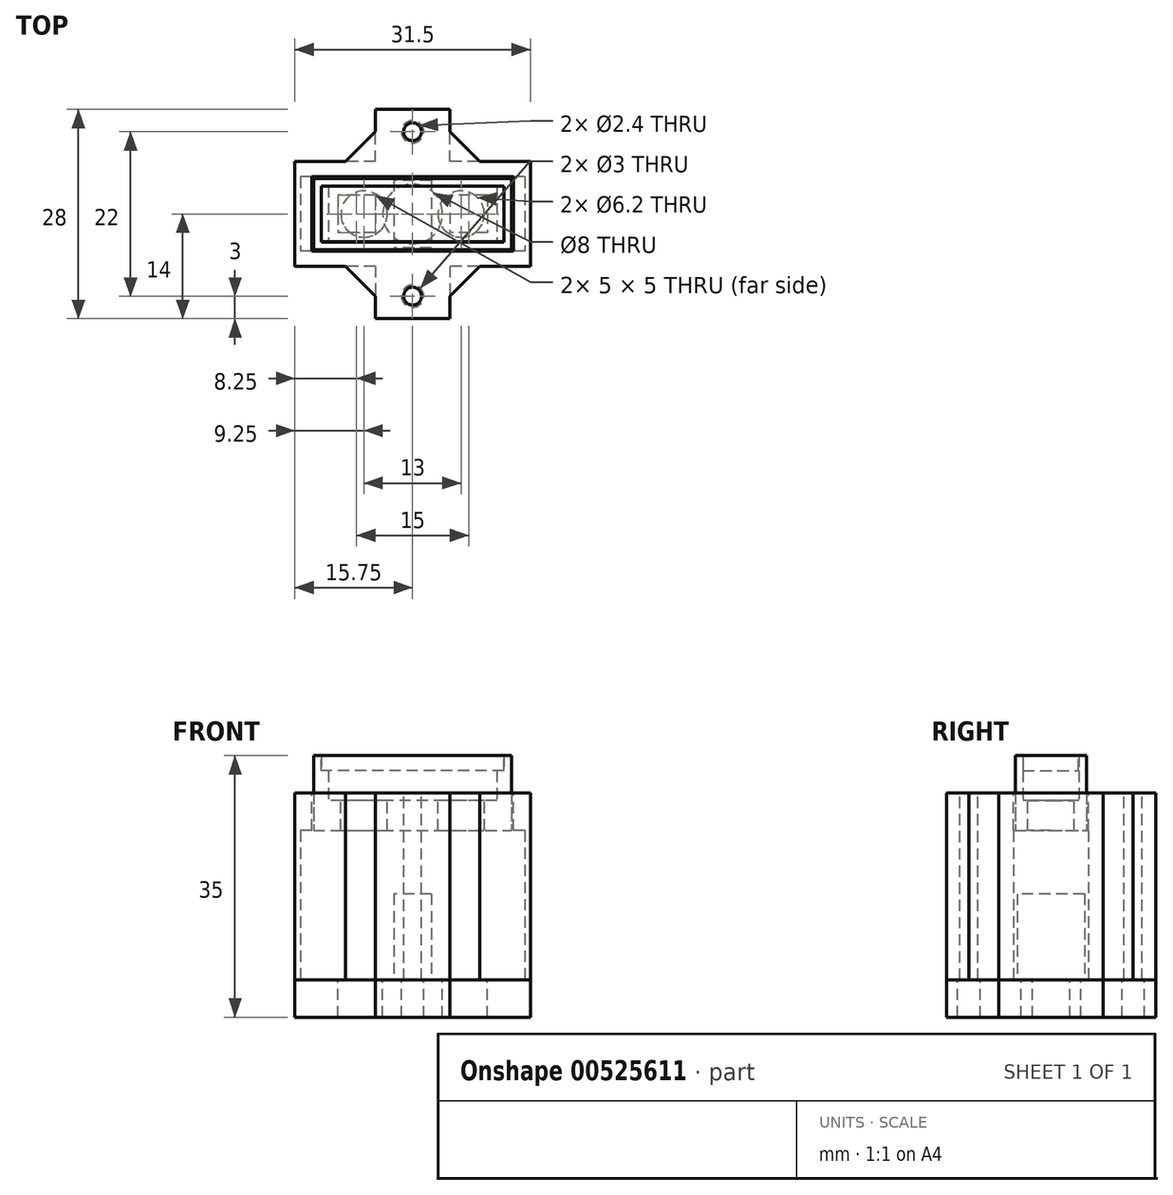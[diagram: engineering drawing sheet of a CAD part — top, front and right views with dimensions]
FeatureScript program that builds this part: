
annotation { "Feature Type Name" : "Feature", "Feature Type Description" : "" }
export const myFeature = defineFeature(function(context is Context, id is Id, definition is map)
    precondition{}
    {
        {
            var Q0;
            Q0=qCreatedBy(makeId("Top.planeOp"),FACE);
            var sketch = newSketch(context, id + "F0", { "sketchPlane" : qUnion([Q0])});
            skLineSegment(sketch, "E0.bottom", {"start": v(13.25, -4.75) * mm, "end": v(-13.25, -4.75) * mm});
            skLineSegment(sketch, "E0.top", {"start": v(13.25, 4.75) * mm, "end": v(-13.25, 4.75) * mm});
            skLineSegment(sketch, "E0.left", {"start": v(13.25, -4.75) * mm, "end": v(13.25, 4.75) * mm});
            skLineSegment(sketch, "E0.right", {"start": v(-13.25, -4.75) * mm, "end": v(-13.25, 4.75) * mm});
            skPoint(sketch, "E0.middle", {"position": v(0, 0) * mm});
            skSolve(sketch);
        }
        {
            var Q0;
            Q0=qSketchRegion(id+"F0",true);
            extrude(context, id + "F1", {"entities" : qUnion([Q0]), "depth" : 13 * mm, "offsetDistance" : 25 * mm});
        }
        {
            var Q0;
            Q0=makeQuery(id+"F1.opExtrude","CAP_FACE",FACE,{"disambiguationData":[OSD([sQuery(id+"F0.wireOp",EDGE,"E0.bottom"),sQuery(id+"F0.wireOp",EDGE,"E0.top"),sQuery(id+"F0.wireOp",EDGE,"E0.left"),sQuery(id+"F0.wireOp",EDGE,"E0.right")])],"isStart":false});
            var sketch = newSketch(context, id + "F2", { "sketchPlane" : qUnion([Q0])});
            skLineSegment(sketch, "E1.bottom", {"start": v(13.25, -4.75) * mm, "end": v(-13.25, -4.75) * mm});
            skLineSegment(sketch, "E1.top", {"start": v(13.25, 4.75) * mm, "end": v(-13.25, 4.75) * mm});
            skLineSegment(sketch, "E1.left", {"start": v(13.25, -4.75) * mm, "end": v(13.25, 4.75) * mm});
            skLineSegment(sketch, "E1.right", {"start": v(-13.25, -4.75) * mm, "end": v(-13.25, 4.75) * mm});
            skPoint(sketch, "E1.middle", {"position": v(0, 0) * mm});
            skLineSegment(sketch, "E2.bottom", {"start": v(12.25, -3.75) * mm, "end": v(-12.25, -3.75) * mm});
            skLineSegment(sketch, "E2.top", {"start": v(12.25, 3.75) * mm, "end": v(-12.25, 3.75) * mm});
            skLineSegment(sketch, "E2.left", {"start": v(12.25, -3.75) * mm, "end": v(12.25, 3.75) * mm});
            skLineSegment(sketch, "E2.right", {"start": v(-12.25, -3.75) * mm, "end": v(-12.25, 3.75) * mm});
            skSolve(sketch);
        }
        {
            var Q0;
            Q0=qSketchRegion(id+"F2",true);
            extrude(context, id + "F3", {"entities" : qUnion([Q0]), "operationType" : NewBodyOperationType.ADD, "depth" : 6 * mm, "offsetDistance" : 25 * mm});
        }
        {
            var Q0;
            Q0=makeQuery(id+"F1.opExtrude","CAP_FACE",FACE,{"disambiguationData":[OSD([sQuery(id+"F0.wireOp",EDGE,"E0.bottom"),sQuery(id+"F0.wireOp",EDGE,"E0.top"),sQuery(id+"F0.wireOp",EDGE,"E0.left"),sQuery(id+"F0.wireOp",EDGE,"E0.right")])],"isStart":false});
            var sketch = newSketch(context, id + "F4", { "sketchPlane" : qUnion([Q0])});
            skLineSegment(sketch, "E3.bottom", {"start": v(-12.25, 3.75) * mm, "end": v(-11.25, 3.75) * mm});
            skLineSegment(sketch, "E3.top", {"start": v(-12.25, -3.75) * mm, "end": v(-11.25, -3.75) * mm});
            skLineSegment(sketch, "E3.left", {"start": v(-12.25, 3.75) * mm, "end": v(-12.25, -3.75) * mm});
            skLineSegment(sketch, "E3.right", {"start": v(-11.25, 3.75) * mm, "end": v(-11.25, -3.75) * mm});
            skLineSegment(sketch, "E4.bottom", {"start": v(12.25, 3.75) * mm, "end": v(11.25, 3.75) * mm});
            skLineSegment(sketch, "E4.top", {"start": v(12.25, -3.75) * mm, "end": v(11.25, -3.75) * mm});
            skLineSegment(sketch, "E4.left", {"start": v(12.25, 3.75) * mm, "end": v(12.25, -3.75) * mm});
            skLineSegment(sketch, "E4.right", {"start": v(11.25, 3.75) * mm, "end": v(11.25, -3.75) * mm});
            skSolve(sketch);
        }
        {
            var Q0;
            Q0=qSketchRegion(id+"F4",true);
            extrude(context, id + "F5", {"entities" : qUnion([Q0]), "operationType" : NewBodyOperationType.ADD, "depth" : 4 * mm, "offsetDistance" : 25 * mm});
        }
        {
            var Q0;
            Q0=makeQuery(id+"F1.opExtrude","CAP_FACE",FACE,{"disambiguationData":[OSD([sQuery(id+"F0.wireOp",EDGE,"E0.bottom"),sQuery(id+"F0.wireOp",EDGE,"E0.top"),sQuery(id+"F0.wireOp",EDGE,"E0.left"),sQuery(id+"F0.wireOp",EDGE,"E0.right")])],"isStart":false});
            var sketch = newSketch(context, id + "F6", { "sketchPlane" : qUnion([Q0])});
            skCircle(sketch, "E5", {"center": v(-6.5, 0) * mm, "radius": 3.1 * mm});
            skCircle(sketch, "E6", {"center": v(6.5, 0) * mm, "radius": 3.1 * mm});
            skSolve(sketch);
        }
        {
            var Q0;
            Q0=qSketchRegion(id+"F6",true);
            extrude(context, id + "F7", {"entities" : qUnion([Q0]), "operationType" : NewBodyOperationType.REMOVE, "oppositeDirection" : true, "depth" : 19 * mm, "offsetDistance" : 25 * mm});
        }
        {
            var Q0;
            Q0=makeQuery(id+"F1.opExtrude","CAP_FACE",FACE,{"disambiguationData":[OSD([sQuery(id+"F0.wireOp",EDGE,"E0.bottom"),sQuery(id+"F0.wireOp",EDGE,"E0.top"),sQuery(id+"F0.wireOp",EDGE,"E0.left"),sQuery(id+"F0.wireOp",EDGE,"E0.right")])],"isStart":true});
            var sketch = newSketch(context, id + "F8", { "sketchPlane" : qUnion([Q0])});
            skLineSegment(sketch, "E7.bottom", {"start": v(-13.25, -4.75) * mm, "end": v(-14.75, -4.75) * mm});
            skLineSegment(sketch, "E7.top", {"start": v(-13.25, 4.75) * mm, "end": v(-14.75, 4.75) * mm});
            skLineSegment(sketch, "E7.left", {"start": v(-13.25, -4.75) * mm, "end": v(-13.25, 4.75) * mm});
            skLineSegment(sketch, "E7.right", {"start": v(-14.75, -4.75) * mm, "end": v(-14.75, 4.75) * mm});
            skLineSegment(sketch, "E8.bottom", {"start": v(13.25, -4.75) * mm, "end": v(14.75, -4.75) * mm});
            skLineSegment(sketch, "E8.top", {"start": v(13.25, 4.75) * mm, "end": v(14.75, 4.75) * mm});
            skLineSegment(sketch, "E8.left", {"start": v(13.25, -4.75) * mm, "end": v(13.25, 4.75) * mm});
            skLineSegment(sketch, "E8.right", {"start": v(14.75, -4.75) * mm, "end": v(14.75, 4.75) * mm});
            skSolve(sketch);
        }
        {
            var Q0;
            Q0=qSketchRegion(id+"F8",true);
            extrude(context, id + "F9", {"entities" : qUnion([Q0]), "operationType" : NewBodyOperationType.ADD, "oppositeDirection" : true, "depth" : 9 * mm, "offsetDistance" : 25 * mm});
        }
        {
            var Q0;
            Q0=makeQuery(id+"F9.boolean.opBoolean","MERGE",FACE,{"derivedFrom":[makeQuery(id+"F1.opExtrude","CAP_FACE",FACE,{"disambiguationData":[OSD([sQuery(id+"F0.wireOp",EDGE,"E0.bottom"),sQuery(id+"F0.wireOp",EDGE,"E0.top"),sQuery(id+"F0.wireOp",EDGE,"E0.left"),sQuery(id+"F0.wireOp",EDGE,"E0.right")])],"isStart":true}),makeQuery(id+"F9.opExtrude","CAP_FACE",FACE,{"disambiguationData":[OSD([sQuery(id+"F8.wireOp",EDGE,"E7.bottom"),sQuery(id+"F8.wireOp",EDGE,"E7.top"),sQuery(id+"F8.wireOp",EDGE,"E7.left"),sQuery(id+"F8.wireOp",EDGE,"E7.right")])],"isStart":true}),makeQuery(id+"F9.opExtrude","CAP_FACE",FACE,{"disambiguationData":[OSD([sQuery(id+"F8.wireOp",EDGE,"E8.bottom"),sQuery(id+"F8.wireOp",EDGE,"E8.top"),sQuery(id+"F8.wireOp",EDGE,"E8.left"),sQuery(id+"F8.wireOp",EDGE,"E8.right")])],"isStart":true})]});
            var sketch = newSketch(context, id + "F10", { "sketchPlane" : qUnion([Q0])});
            skCircle(sketch, "E9", {"center": v(0, 0) * mm, "radius": 2.55 * mm});
            skSolve(sketch);
        }
        {
            var Q0;
            Q0=qSketchRegion(id+"F10",true);
            extrude(context, id + "F11", {"entities" : qUnion([Q0]), "operationType" : NewBodyOperationType.REMOVE, "oppositeDirection" : true, "depth" : 3 * mm, "offsetDistance" : 25 * mm});
        }
        {
            var Q0;
            Q0=qCreatedBy(makeId("Top.planeOp"),FACE);
            cPlane(context, id + "F12", {"entities" : qUnion([Q0]), "cplaneType" : CPlaneType.OFFSET, "offset" : 14 * mm, "width" : 150 * mm, "height" : 150 * mm});
        }
        {
            var Q0;
            Q0=qCreatedBy(id+"F12.planeOp",FACE);
            var sketch = newSketch(context, id + "F13", { "sketchPlane" : qUnion([Q0])});
            skLineSegment(sketch, "E10.bottom", {"start": v(15.75, -7) * mm, "end": v(-15.75, -7) * mm});
            skLineSegment(sketch, "E10.top", {"start": v(15.75, 7) * mm, "end": v(-15.75, 7) * mm});
            skLineSegment(sketch, "E10.left", {"start": v(15.75, -7) * mm, "end": v(15.75, 7) * mm});
            skLineSegment(sketch, "E10.right", {"start": v(-15.75, -7) * mm, "end": v(-15.75, 7) * mm});
            skPoint(sketch, "E10.middle", {"position": v(0, 0) * mm});
            skLineSegment(sketch, "E11.bottom", {"start": v(-5, 7) * mm, "end": v(5, 7) * mm});
            skLineSegment(sketch, "E11.top", {"start": v(-5, 14) * mm, "end": v(5, 14) * mm});
            skLineSegment(sketch, "E11.left", {"start": v(-5, 7) * mm, "end": v(-5, 14) * mm});
            skLineSegment(sketch, "E11.right", {"start": v(5, 7) * mm, "end": v(5, 14) * mm});
            skLineSegment(sketch, "E12.bottom", {"start": v(-5, -7) * mm, "end": v(5, -7) * mm});
            skLineSegment(sketch, "E12.top", {"start": v(-5, -14) * mm, "end": v(5, -14) * mm});
            skLineSegment(sketch, "E12.left", {"start": v(-5, -7) * mm, "end": v(-5, -14) * mm});
            skLineSegment(sketch, "E12.right", {"start": v(5, -7) * mm, "end": v(5, -14) * mm});
            skLineSegment(sketch, "E13.bottom", {"start": v(13.5, -5) * mm, "end": v(-13.5, -5) * mm});
            skLineSegment(sketch, "E13.top", {"start": v(13.5, 5) * mm, "end": v(-13.5, 5) * mm});
            skLineSegment(sketch, "E13.left", {"start": v(13.5, -5) * mm, "end": v(13.5, 5) * mm});
            skLineSegment(sketch, "E13.right", {"start": v(-13.5, -5) * mm, "end": v(-13.5, 5) * mm});
            skSolve(sketch);
        }
        {
            var Q0;
            Q0=qSketchRegion(id+"F13",true);
            extrude(context, id + "F14", {"entities" : qUnion([Q0]), "oppositeDirection" : true, "depth" : 25 * mm, "offsetDistance" : 25 * mm});
        }
        {
            var Q0;
            Q0=makeQuery(id+"F14.opExtrude","CAP_FACE",FACE,{"disambiguationData":[OSD([sQuery(id+"F13.wireOp",EDGE,"E10.bottom"),sQuery(id+"F13.wireOp",EDGE,"E10.top"),sQuery(id+"F13.wireOp",EDGE,"E10.left"),sQuery(id+"F13.wireOp",EDGE,"E10.right"),sQuery(id+"F13.wireOp",EDGE,"E11.top"),sQuery(id+"F13.wireOp",EDGE,"E11.left"),sQuery(id+"F13.wireOp",EDGE,"E11.right"),sQuery(id+"F13.wireOp",EDGE,"E12.top"),sQuery(id+"F13.wireOp",EDGE,"E12.left"),sQuery(id+"F13.wireOp",EDGE,"E12.right")])],"isStart":false});
            var sketch = newSketch(context, id + "F15", { "sketchPlane" : qUnion([Q0])});
            skLineSegment(sketch, "E14.bottom", {"start": v(15, -5) * mm, "end": v(-15, -5) * mm});
            skLineSegment(sketch, "E14.top", {"start": v(15, 5) * mm, "end": v(-15, 5) * mm});
            skLineSegment(sketch, "E14.left", {"start": v(15, -5) * mm, "end": v(15, 5) * mm});
            skLineSegment(sketch, "E14.right", {"start": v(-15, -5) * mm, "end": v(-15, 5) * mm});
            skPoint(sketch, "E14.middle", {"position": v(0, 0) * mm});
            skSolve(sketch);
        }
        {
            var Q0;
            Q0 = qSketchRegion(id + "F15", true);
            extrude(context, id + "F16", {"entities" : qUnion([Q0]), "operationType" : NewBodyOperationType.REMOVE, "oppositeDirection" : true, "depth" : 20 * mm, "offsetDistance" : 25 * mm});
        }
        {
            var Q0;
            Q0=makeQuery(id+"F14.opExtrude","CAP_FACE",FACE,{"disambiguationData":[OSD([sQuery(id+"F13.wireOp",EDGE,"E10.bottom"),sQuery(id+"F13.wireOp",EDGE,"E10.top"),sQuery(id+"F13.wireOp",EDGE,"E10.left"),sQuery(id+"F13.wireOp",EDGE,"E10.right"),sQuery(id+"F13.wireOp",EDGE,"E11.top"),sQuery(id+"F13.wireOp",EDGE,"E11.left"),sQuery(id+"F13.wireOp",EDGE,"E11.right"),sQuery(id+"F13.wireOp",EDGE,"E12.top"),sQuery(id+"F13.wireOp",EDGE,"E12.left"),sQuery(id+"F13.wireOp",EDGE,"E12.right")])],"isStart":true});
            var sketch = newSketch(context, id + "F17", { "sketchPlane" : qUnion([Q0])});
            skCircle(sketch, "E15", {"center": v(0, 11) * mm, "radius": 1.2 * mm});
            skCircle(sketch, "E16", {"center": v(0, -11) * mm, "radius": 1.2 * mm});
            skSolve(sketch);
        }
        {
            var Q0;
            Q0 = qSketchRegion(id + "F17", true);
            extrude(context, id + "F18", {"entities" : qUnion([Q0]), "operationType" : NewBodyOperationType.REMOVE, "oppositeDirection" : true, "depth" : 25 * mm, "offsetDistance" : 25 * mm});
        }
        {
            var Q0;
            Q0=makeQuery(id+"F14.opExtrude","CAP_FACE",FACE,{"disambiguationData":[OSD([sQuery(id+"F13.wireOp",EDGE,"E10.bottom"),sQuery(id+"F13.wireOp",EDGE,"E10.top"),sQuery(id+"F13.wireOp",EDGE,"E10.left"),sQuery(id+"F13.wireOp",EDGE,"E10.right"),sQuery(id+"F13.wireOp",EDGE,"E11.top"),sQuery(id+"F13.wireOp",EDGE,"E11.left"),sQuery(id+"F13.wireOp",EDGE,"E11.right"),sQuery(id+"F13.wireOp",EDGE,"E12.top"),sQuery(id+"F13.wireOp",EDGE,"E12.left"),sQuery(id+"F13.wireOp",EDGE,"E12.right"),sQuery(id+"F13.wireOp",EDGE,"E13.bottom"),sQuery(id+"F13.wireOp",EDGE,"E13.top"),sQuery(id+"F13.wireOp",EDGE,"E13.left"),sQuery(id+"F13.wireOp",EDGE,"E13.right")])],"isStart":false});
            var sketch = newSketch(context, id + "F19", { "sketchPlane" : qUnion([Q0])});
            skLineSegment(sketch, "E17.bottom", {"start": v(15.75, -7) * mm, "end": v(-15.75, -7) * mm});
            skLineSegment(sketch, "E17.top", {"start": v(15.75, 7) * mm, "end": v(-15.75, 7) * mm});
            skLineSegment(sketch, "E17.left", {"start": v(15.75, -7) * mm, "end": v(15.75, 7) * mm});
            skLineSegment(sketch, "E17.right", {"start": v(-15.75, -7) * mm, "end": v(-15.75, 7) * mm});
            skPoint(sketch, "E17.middle", {"position": v(0, 0) * mm});
            skLineSegment(sketch, "E18.bottom", {"start": v(-5, 7) * mm, "end": v(5, 7) * mm});
            skLineSegment(sketch, "E18.top", {"start": v(-5, 14) * mm, "end": v(5, 14) * mm});
            skLineSegment(sketch, "E18.left", {"start": v(-5, 7) * mm, "end": v(-5, 14) * mm});
            skLineSegment(sketch, "E18.right", {"start": v(5, 7) * mm, "end": v(5, 14) * mm});
            skLineSegment(sketch, "E19.bottom", {"start": v(5, -7) * mm, "end": v(-5, -7) * mm});
            skLineSegment(sketch, "E19.top", {"start": v(5, -14) * mm, "end": v(-5, -14) * mm});
            skLineSegment(sketch, "E19.left", {"start": v(5, -7) * mm, "end": v(5, -14) * mm});
            skLineSegment(sketch, "E19.right", {"start": v(-5, -7) * mm, "end": v(-5, -14) * mm});
            skCircle(sketch, "E20", {"center": v(0, 0) * mm, "radius": 4 * mm});
            skLineSegment(sketch, "E21.bottom", {"start": v(-5, -2.5) * mm, "end": v(-10, -2.5) * mm});
            skLineSegment(sketch, "E21.top", {"start": v(-5, 2.5) * mm, "end": v(-10, 2.5) * mm});
            skLineSegment(sketch, "E21.left", {"start": v(-5, -2.5) * mm, "end": v(-5, 2.5) * mm});
            skLineSegment(sketch, "E21.right", {"start": v(-10, -2.5) * mm, "end": v(-10, 2.5) * mm});
            skPoint(sketch, "E21.middle", {"position": v(-7.5, 0) * mm});
            skLineSegment(sketch, "E22.bottom", {"start": v(10, -2.5) * mm, "end": v(5, -2.5) * mm});
            skLineSegment(sketch, "E22.top", {"start": v(10, 2.5) * mm, "end": v(5, 2.5) * mm});
            skLineSegment(sketch, "E22.left", {"start": v(10, -2.5) * mm, "end": v(10, 2.5) * mm});
            skLineSegment(sketch, "E22.right", {"start": v(5, -2.5) * mm, "end": v(5, 2.5) * mm});
            skPoint(sketch, "E22.middle", {"position": v(7.5, 0) * mm});
            skCircle(sketch, "E23", {"center": v(0, 11) * mm, "radius": 1.5 * mm});
            skCircle(sketch, "E24", {"center": v(0, -11) * mm, "radius": 1.5 * mm});
            skSolve(sketch);
        }
        {
            var Q0;
            Q0 = qSketchRegion(id + "F19", true);
            extrude(context, id + "F20", {"entities" : qUnion([Q0]), "depth" : 5 * mm, "offsetDistance" : 25 * mm});
        }
        {
            var Q0;
            Q0=makeQuery(id+"F14.opExtrude","SWEPT_EDGE",EDGE,{"disambiguationData":[OSD([sQuery(id+"F13.wireOp",EDGE,"E10.top"),sQuery(id+"F13.wireOp",EDGE,"E11.bottom"),sQuery(id+"F13.wireOp",EDGE,"E11.left")])]});
            var Q1;
            Q1=makeQuery(id+"F14.opExtrude","SWEPT_EDGE",EDGE,{"disambiguationData":[OSD([sQuery(id+"F13.wireOp",EDGE,"E10.top"),sQuery(id+"F13.wireOp",EDGE,"E11.bottom"),sQuery(id+"F13.wireOp",EDGE,"E11.right")])]});
            var Q2;
            Q2=makeQuery(id+"F14.opExtrude","SWEPT_EDGE",EDGE,{"disambiguationData":[OSD([sQuery(id+"F13.wireOp",EDGE,"E10.bottom"),sQuery(id+"F13.wireOp",EDGE,"E12.bottom"),sQuery(id+"F13.wireOp",EDGE,"E12.right")])]});
            var Q3;
            Q3=makeQuery(id+"F14.opExtrude","SWEPT_EDGE",EDGE,{"disambiguationData":[OSD([sQuery(id+"F13.wireOp",EDGE,"E10.bottom"),sQuery(id+"F13.wireOp",EDGE,"E12.bottom"),sQuery(id+"F13.wireOp",EDGE,"E12.left")])]});
            chamfer(context, id + "F21", {"entities" : qUnion([Q0, Q1, Q2, Q3]), "width" : 4 * mm, "tangentPropagation" : true});
        }
        {
            var Q0;
            Q0=makeQuery(id+"F14.opExtrude","CAP_FACE",FACE,{"disambiguationData":[OSD([sQuery(id+"F13.wireOp",EDGE,"E10.bottom"),sQuery(id+"F13.wireOp",EDGE,"E10.top"),sQuery(id+"F13.wireOp",EDGE,"E10.left"),sQuery(id+"F13.wireOp",EDGE,"E10.right"),sQuery(id+"F13.wireOp",EDGE,"E11.top"),sQuery(id+"F13.wireOp",EDGE,"E11.left"),sQuery(id+"F13.wireOp",EDGE,"E11.right"),sQuery(id+"F13.wireOp",EDGE,"E12.top"),sQuery(id+"F13.wireOp",EDGE,"E12.left"),sQuery(id+"F13.wireOp",EDGE,"E12.right"),sQuery(id+"F13.wireOp",EDGE,"E13.bottom"),sQuery(id+"F13.wireOp",EDGE,"E13.top"),sQuery(id+"F13.wireOp",EDGE,"E13.left"),sQuery(id+"F13.wireOp",EDGE,"E13.right")])],"isStart":false});
            cPlane(context, id + "F22", {"entities" : qUnion([Q0]), "cplaneType" : CPlaneType.OFFSET, "offset" : 0 * mm, "width" : 150 * mm, "height" : 150 * mm});
        }
        {
            var Q0;
            Q0=qCreatedBy(id+"F22.planeOp",FACE);
            var sketch = newSketch(context, id + "F23", { "sketchPlane" : qUnion([Q0])});
            skLineSegment(sketch, "E25.bottom", {"start": v(2.5, -4.5) * mm, "end": v(-2.5, -4.5) * mm});
            skLineSegment(sketch, "E25.top", {"start": v(2.5, 4.5) * mm, "end": v(-2.5, 4.5) * mm});
            skLineSegment(sketch, "E25.left", {"start": v(2.5, -4.5) * mm, "end": v(2.5, 4.5) * mm});
            skLineSegment(sketch, "E25.right", {"start": v(-2.5, -4.5) * mm, "end": v(-2.5, 4.5) * mm});
            skPoint(sketch, "E25.middle", {"position": v(0, 0) * mm});
            skLineSegment(sketch, "E26.0", {"start": v(15, 5) * mm, "end": v(-15, 5) * mm});
            skLineSegment(sketch, "E26.1", {"start": v(15, -5) * mm, "end": v(-15, -5) * mm});
            skPoint(sketch, "E27", {"position": v(0, 5) * mm});
            skSolve(sketch);
        }
        {
            var Q0;
            Q0 = qSketchRegion(id + "F23", true);
            extrude(context, id + "F24", {"entities" : qUnion([Q0]), "oppositeDirection" : true, "depth" : 11.5 * mm, "offsetDistance" : 25 * mm});
        }
        {
            var Q0;
            Q0=makeQuery(id+"F3.opExtrude","CAP_FACE",FACE,{"disambiguationData":[OSD([sQuery(id+"F2.wireOp",EDGE,"E1.bottom"),sQuery(id+"F2.wireOp",EDGE,"E1.top"),sQuery(id+"F2.wireOp",EDGE,"E1.left"),sQuery(id+"F2.wireOp",EDGE,"E1.right"),sQuery(id+"F2.wireOp",EDGE,"E2.bottom"),sQuery(id+"F2.wireOp",EDGE,"E2.top"),sQuery(id+"F2.wireOp",EDGE,"E2.left"),sQuery(id+"F2.wireOp",EDGE,"E2.right")])],"isStart":false});
            var sketch = newSketch(context, id + "F25", { "sketchPlane" : qUnion([Q0])});
            skLineSegment(sketch, "E28.bottom", {"start": v(12.2, -3.7) * mm, "end": v(-12.2, -3.7) * mm});
            skLineSegment(sketch, "E28.top", {"start": v(12.2, 3.7) * mm, "end": v(-12.2, 3.7) * mm});
            skLineSegment(sketch, "E28.left", {"start": v(12.2, -3.7) * mm, "end": v(12.2, 3.7) * mm});
            skLineSegment(sketch, "E28.right", {"start": v(-12.2, -3.7) * mm, "end": v(-12.2, 3.7) * mm});
            skPoint(sketch, "E28.middle", {"position": v(0, 0) * mm});
            skPoint(sketch, "E28.middle.positionSnap0", {"position": v(-12.25, 0) * mm});
            skPoint(sketch, "E28.middle.positionSnap1", {"position": v(0, 3.75) * mm});
            skPoint(sketch, "E28.centerSnap0", {"position": v(-12.25, 0) * mm});
            skPoint(sketch, "E28.centerSnap1", {"position": v(0, 3.75) * mm});
            skSolve(sketch);
        }
        {
            var Q0;
            Q0 = qSketchRegion(id + "F25", true);
            extrude(context, id + "F26", {"entities" : qUnion([Q0]), "oppositeDirection" : true, "depth" : 2 * mm, "offsetDistance" : 25 * mm});
        }
    });
